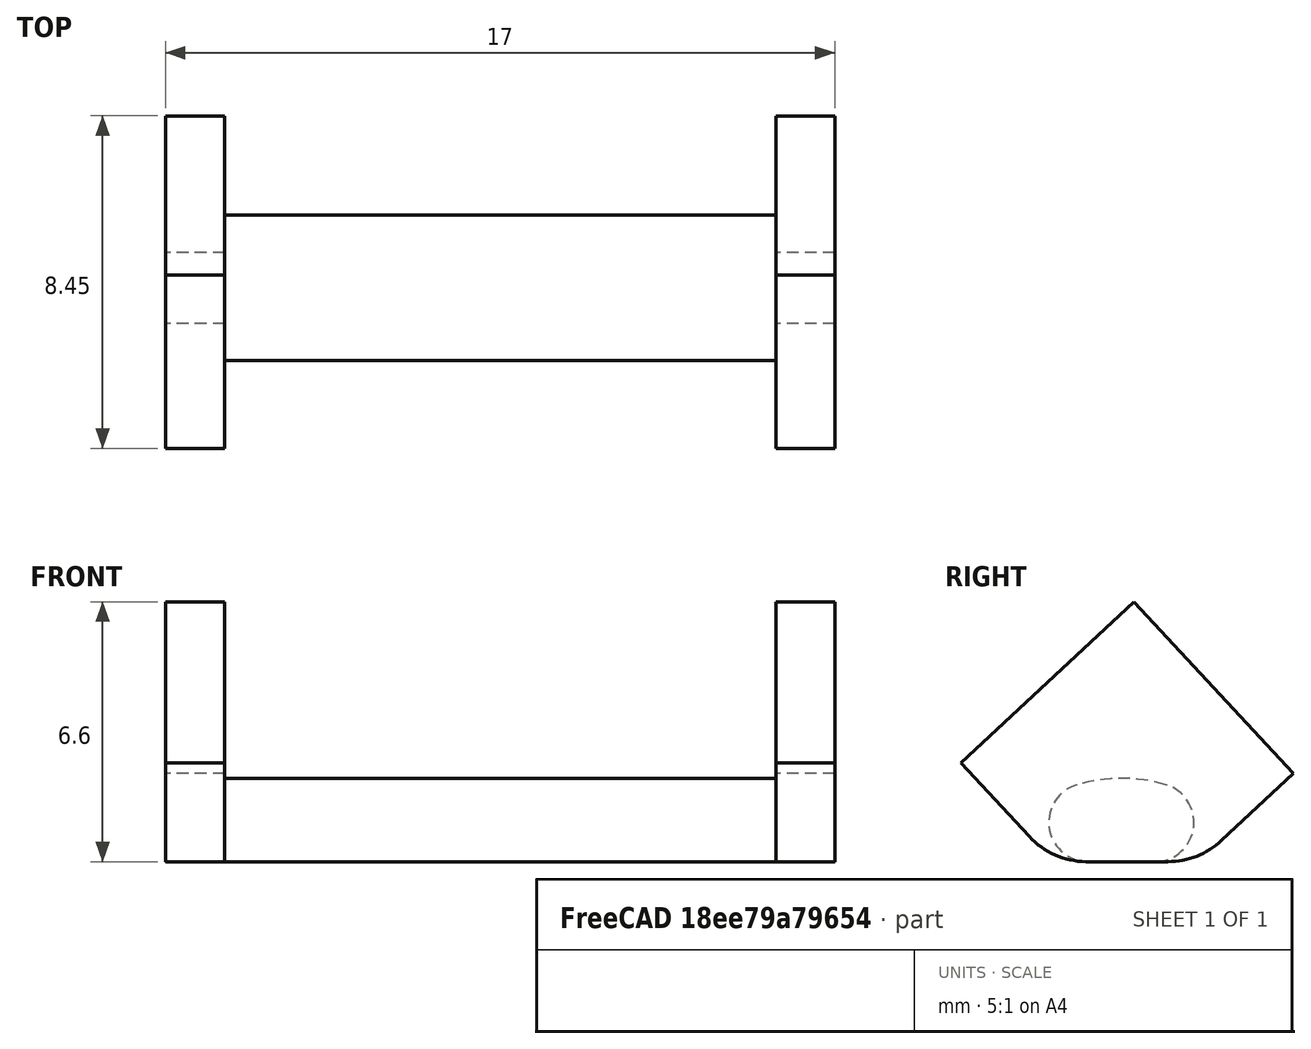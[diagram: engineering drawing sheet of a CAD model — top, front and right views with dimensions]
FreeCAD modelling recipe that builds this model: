
FCSTD DOCUMENT  (FreeCAD 0.18.4R)
Label: CableClip3
License: All rights reserved
LicenseURL: http://en.wikipedia.org/wiki/All_rights_reserved
objects: Part::Fillet×6, Sketcher::SketchObject×3, PartDesign::Pad×3, Part::MultiFuse×1, Mesh::Feature×1
note: 16 computed .brp shape members not serialized (recipe doc carries the construction recipe); baked Part::Feature solids carry a one-line shape summary decoded from their .brp

FEATURE [Sketcher::SketchObject] Sketch
  MapMode = 5
  sketch-geometry (2):
    g0: ArcOfCircle CenterX=0 CenterY=0 CenterZ=0 NormalX=0 NormalY=0 NormalZ=1 AngleXU=0 Radius=3.98869 StartAngle=4.37951 EndAngle=6.54674
    g1: LineSegment StartX=-1.30335 StartY=-3.76973 StartZ=0 EndX=3.85096 EndY=1.0391 EndZ=0
  constraints (2):
    c: Coincident(g1,g0)
    c: Coincident(g1,g0)
FEATURE [PartDesign::Pad] Pad
  Length = 17
  Length2 = 100
  Profile = -> Sketch
  Type = 0
FEATURE [Sketcher::SketchObject] Sketch002
  MapMode = 5
  Placement = pos=(0,0,15.5) rot=(0,0,1;0rad)
  sketch-geometry (5):
    g0: LineSegment StartX=-0.001379 StartY=-2.55738 StartZ=0 EndX=2.7143 EndY=-0.023327 EndZ=0
    g1: LineSegment StartX=-0.001379 StartY=-2.55738 StartZ=0 EndX=0.005451 EndY=-5.98313 EndZ=0
    g2: LineSegment StartX=5.99589 StartY=-0.02429 StartZ=0 EndX=6.01059 EndY=-5.97801 EndZ=0
    g3: LineSegment StartX=0.005451 StartY=-5.98313 StartZ=0 EndX=6.01059 EndY=-5.97801 EndZ=0
    g4: LineSegment StartX=2.7143 StartY=-0.023327 StartZ=0 EndX=5.99589 EndY=-0.02429 EndZ=0
  constraints (5):
    c: Coincident(g1,g0)
    c: Coincident(g1,g3)
    c: Coincident(g4,g0)
    c: Coincident(g4,g2)
    c: Coincident(g2,g3)
FEATURE [PartDesign::Pad] Pad002
  Length = 1.5
  Length2 = 100
  Placement = pos=(0,0,15.5) rot=(0,0,1;0rad)
  Profile = -> Sketch002
  Type = 0
FEATURE [Part::Fillet] Fillet
  Base = -> Pad
  Edges = 1 edges r=1: [Edge1]
FEATURE [Part::Fillet] Fillet001
  Base = -> Fillet
  Edges = 1 edges r=1: [Edge3]
  Placement = pos=(0,0,0) rot=(0,0,1;0.820305rad)
FEATURE [Part::Fillet] Fillet004
  Base = -> Pad002
  Edges = 1 edges r=2: [Edge1]
FEATURE [Part::Fillet] Fillet005
  Base = -> Fillet004
  Edges = 1 edges r=2: [Edge3]
  Placement = pos=(0,0,0) rot=(0,0,1;0.820305rad)
FEATURE [Sketcher::SketchObject] Sketch003
  MapMode = 5
  Placement = pos=(0,0,16) rot=(0,0,1;0rad)
  sketch-geometry (5):
    g0: LineSegment StartX=-0.001379 StartY=-2.55738 StartZ=0 EndX=2.7143 EndY=-0.023327 EndZ=0
    g1: LineSegment StartX=-0.001379 StartY=-2.55738 StartZ=0 EndX=0.005451 EndY=-5.98313 EndZ=0
    g2: LineSegment StartX=5.99589 StartY=-0.02429 StartZ=0 EndX=6.01059 EndY=-5.97801 EndZ=0
    g3: LineSegment StartX=0.005451 StartY=-5.98313 StartZ=0 EndX=6.01059 EndY=-5.97801 EndZ=0
    g4: LineSegment StartX=2.7143 StartY=-0.023327 StartZ=0 EndX=5.99589 EndY=-0.02429 EndZ=0
  constraints (5):
    c: Coincident(g1,g0)
    c: Coincident(g1,g3)
    c: Coincident(g4,g0)
    c: Coincident(g4,g2)
    c: Coincident(g2,g3)
FEATURE [PartDesign::Pad] Pad003
  Length = 1.5
  Length2 = 100
  Placement = pos=(0,0,16) rot=(0,0,1;0rad)
  Profile = -> Sketch003
  Type = 0
FEATURE [Part::Fillet] Fillet006
  Base = -> Pad003
  Edges = 1 edges r=2: [Edge1]
FEATURE [Part::Fillet] Fillet007
  Base = -> Fillet006
  Edges = 1 edges r=2: [Edge3]
  Placement = pos=(0,0,-16) rot=(0,0,1;0.820305rad)
FEATURE [Part::MultiFuse] Fusion
  Placement = pos=(0,0,0) rot=(0,1,0;-1.5708rad)
  Shapes = -> [Fillet005,Fillet007,Fillet001]
FEATURE [Mesh::Feature] Mesh  label="Fusion (Meshed)"
